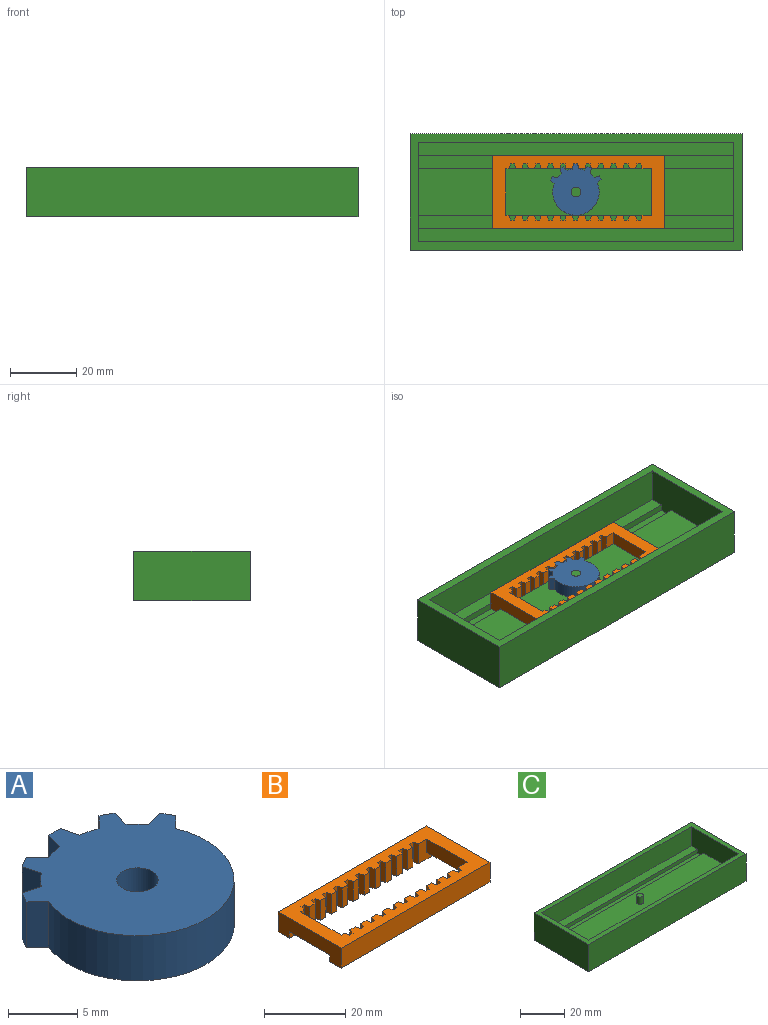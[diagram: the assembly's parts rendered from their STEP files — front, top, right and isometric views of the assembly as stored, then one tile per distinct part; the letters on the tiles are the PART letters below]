
ASSEMBLY  parts=3 mates=4
PART A: 23 faces, bbox 15.3x15.5x4 mm
  f0: plane 15.5x15.29mm, normal (0,0,1), area 158.9mm2, adj f1,f2,f3,f4,f5,f6,f7,f8
  f1: cylinder r=7mm len=14mm, axis (0,0,-1), area 109.3mm2, adj f0,f2,f20,f21
  f2: plane 4x1.14mm, normal (0.7,-0.72,0), area 6.4mm2, adj f0,f1,f3,f21
  f3: cylinder r=8.5mm len=4mm, axis (0,0,-1), area 4.8mm2, adj f0,f2,f4,f21
  f4: plane 4x1.54mm, normal (-0.27,0.96,0), area 6.4mm2, adj f0,f3,f5,f21
  f5: cylinder r=7mm len=4mm, axis (0,0,-1), area 6.6mm2, adj f0,f4,f6,f21
  f6: plane 4x1.54mm, normal (0.96,-0.27,0), area 6.4mm2, adj f0,f5,f7,f21
  f7: cylinder r=8.5mm len=4mm, axis (0,0,-1), area 4.8mm2, adj f0,f6,f8,f21
  f8: plane 4x1.14mm, normal (-0.72,0.7,0), area 6.4mm2, adj f0,f7,f9,f21
  f9: cylinder r=7mm len=4mm, axis (0,0,-1), area 6.6mm2, adj f0,f8,f10,f21
  f10: plane 4x1.55mm, normal (0.97,0.25,0), area 6.4mm2, adj f0,f9,f11,f21
  f11: cylinder r=8.5mm len=4mm, axis (0,0,-1), area 4.8mm2, adj f0,f10,f12,f21
  f12: plane 4x1.55mm, normal (-0.97,0.25,0), area 6.4mm2, adj f0,f11,f13,f21
  f13: cylinder r=7mm len=4mm, axis (0,0,-1), area 6.6mm2, adj f0,f12,f14,f21
  f14: plane 4x1.14mm, normal (0.72,0.7,0), area 6.4mm2, adj f0,f13,f15,f21
  f15: cylinder r=8.5mm len=4mm, axis (0,0,-1), area 4.8mm2, adj f0,f14,f16,f21
  f16: plane 4x1.54mm, normal (-0.96,-0.27,0), area 6.4mm2, adj f0,f15,f17,f21
  f17: cylinder r=7mm len=4mm, axis (0,0,-1), area 6.6mm2, adj f0,f16,f18,f21
  f18: plane 4x1.54mm, normal (0.27,0.96,0), area 6.4mm2, adj f0,f17,f19,f21
  f19: cylinder r=8.5mm len=4mm, axis (0,0,-1), area 4.8mm2, adj f0,f18,f20,f21
  f20: plane 4x1.14mm, normal (-0.7,-0.72,0), area 6.4mm2, adj f0,f1,f19,f21
  f21: plane 15.5x15.29mm, normal (0,0,-1), area 158.9mm2, adj f1,f2,f3,f4,f5,f6,f7,f8
  f22: cylinder r=1.5mm len=4mm, axis (0,0,-1), area 37.7mm2, adj f0,f21
PART B: 101 faces, bbox 52x22x6 mm
  f0: plane 6.92x6mm, normal (0,1,0), area 25.5mm2, adj f3,f41,f83,f87,f89,f94
  f1: cylinder r=8.5mm len=6mm, axis (0,0,1), area 7.3mm2, adj f2,f3,f41,f89
  f2: plane 6x1.48mm, normal (0.97,0.25,0), area 9.2mm2, adj f1,f4,f41,f89
  f3: plane 6x1.48mm, normal (-0.97,0.25,0), area 9.2mm2, adj f0,f1,f41,f89
  f4: plane 6x1.84mm, normal (0,1,0), area 11mm2, adj f2,f7,f41,f89
  f5: cylinder r=8.5mm len=6mm, axis (0,0,1), area 7.3mm2, adj f6,f7,f41,f89
  f6: plane 6x1.48mm, normal (0.97,0.25,0), area 9.2mm2, adj f5,f40,f41,f89
  f7: plane 6x1.48mm, normal (-0.97,0.25,0), area 9.2mm2, adj f4,f5,f41,f89
  f8: plane 6x1.84mm, normal (0,1,0), area 11mm2, adj f11,f14,f41,f89
  f9: cylinder r=8.5mm len=6mm, axis (0,0,1), area 7.3mm2, adj f10,f11,f41,f89
  f10: plane 6x1.48mm, normal (0.97,0.25,0), area 9.2mm2, adj f9,f41,f89,f91
  f11: plane 6x1.48mm, normal (-0.97,0.25,0), area 9.2mm2, adj f8,f9,f41,f89
  f12: plane 6x1.84mm, normal (0,1,0), area 11mm2, adj f15,f18,f41,f89
  f13: cylinder r=8.5mm len=6mm, axis (0,0,1), area 7.3mm2, adj f14,f15,f41,f89
  f14: plane 6x1.48mm, normal (0.97,0.25,0), area 9.2mm2, adj f8,f13,f41,f89
  f15: plane 6x1.48mm, normal (-0.97,0.25,0), area 9.2mm2, adj f12,f13,f41,f89
  f16: plane 6x1.84mm, normal (0,1,0), area 11mm2, adj f19,f22,f41,f89
  f17: cylinder r=8.5mm len=6mm, axis (0,0,1), area 7.3mm2, adj f18,f19,f41,f89
  f18: plane 6x1.48mm, normal (0.97,0.25,0), area 9.2mm2, adj f12,f17,f41,f89
  f19: plane 6x1.48mm, normal (-0.97,0.25,0), area 9.2mm2, adj f16,f17,f41,f89
  f20: plane 6x1.84mm, normal (0,1,0), area 11mm2, adj f23,f26,f41,f89
  f21: cylinder r=8.5mm len=6mm, axis (0,0,1), area 7.3mm2, adj f22,f23,f41,f89
  f22: plane 6x1.48mm, normal (0.97,0.25,0), area 9.2mm2, adj f16,f21,f41,f89
  f23: plane 6x1.48mm, normal (-0.97,0.25,0), area 9.2mm2, adj f20,f21,f41,f89
  f24: plane 6x1.84mm, normal (0,1,0), area 11mm2, adj f27,f30,f41,f89
  f25: cylinder r=8.5mm len=6mm, axis (0,0,1), area 7.3mm2, adj f26,f27,f41,f89
  f26: plane 6x1.48mm, normal (0.97,0.25,0), area 9.2mm2, adj f20,f25,f41,f89
  f27: plane 6x1.48mm, normal (-0.97,0.25,0), area 9.2mm2, adj f24,f25,f41,f89
  f28: plane 6x1.84mm, normal (0,1,0), area 11mm2, adj f31,f34,f41,f89
  f29: cylinder r=8.5mm len=6mm, axis (0,0,1), area 7.3mm2, adj f30,f31,f41,f89
  f30: plane 6x1.48mm, normal (0.97,0.25,0), area 9.2mm2, adj f24,f29,f41,f89
  f31: plane 6x1.48mm, normal (-0.97,0.25,0), area 9.2mm2, adj f28,f29,f41,f89
  f32: plane 6x1.84mm, normal (0,1,0), area 11mm2, adj f35,f38,f41,f89
  f33: cylinder r=8.5mm len=6mm, axis (0,0,1), area 7.3mm2, adj f34,f35,f41,f89
  f34: plane 6x1.48mm, normal (0.97,0.25,0), area 9.2mm2, adj f28,f33,f41,f89
  f35: plane 6x1.48mm, normal (-0.97,0.25,0), area 9.2mm2, adj f32,f33,f41,f89
  f36: plane 6x1.84mm, normal (0,1,0), area 11mm2, adj f39,f41,f89,f100
  f37: cylinder r=8.5mm len=6mm, axis (0,0,1), area 7.3mm2, adj f38,f39,f41,f89
  f38: plane 6x1.48mm, normal (0.97,0.25,0), area 9.2mm2, adj f32,f37,f41,f89
  f39: plane 6x1.48mm, normal (-0.97,0.25,0), area 9.2mm2, adj f36,f37,f41,f89
  f40: plane 6x1.84mm, normal (0,1,0), area 11mm2, adj f6,f41,f89,f99
  f41: plane 52x22mm, normal (0,0,1), area 476mm2, adj f0,f1,f2,f3,f4,f5,f6,f7
  f42: plane 6.92x6mm, normal (0,-1,0), area 25.5mm2, adj f41,f45,f83,f84,f87,f94
  f43: cylinder r=8.5mm len=6mm, axis (0,0,1), area 7.3mm2, adj f41,f44,f45,f84
  f44: plane 6x1.48mm, normal (0.97,-0.25,0), area 9.2mm2, adj f41,f43,f46,f84
  f45: plane 6x1.48mm, normal (-0.97,-0.25,0), area 9.2mm2, adj f41,f42,f43,f84
  f46: plane 6x1.84mm, normal (0,-1,0), area 11mm2, adj f41,f44,f49,f84
  f47: cylinder r=8.5mm len=6mm, axis (0,0,1), area 7.3mm2, adj f41,f48,f49,f84
  f48: plane 6x1.48mm, normal (0.97,-0.25,0), area 9.2mm2, adj f41,f47,f82,f84
  f49: plane 6x1.48mm, normal (-0.97,-0.25,0), area 9.2mm2, adj f41,f46,f47,f84
  f50: plane 6x1.84mm, normal (0,-1,0), area 11mm2, adj f41,f53,f56,f84
  f51: cylinder r=8.5mm len=6mm, axis (0,0,1), area 7.3mm2, adj f41,f52,f53,f84
  f52: plane 6x1.48mm, normal (0.97,-0.25,0), area 9.2mm2, adj f41,f51,f84,f90
  f53: plane 6x1.48mm, normal (-0.97,-0.25,0), area 9.2mm2, adj f41,f50,f51,f84
  f54: plane 6x1.84mm, normal (0,-1,0), area 11mm2, adj f41,f57,f60,f84
  f55: cylinder r=8.5mm len=6mm, axis (0,0,1), area 7.3mm2, adj f41,f56,f57,f84
  f56: plane 6x1.48mm, normal (0.97,-0.25,0), area 9.2mm2, adj f41,f50,f55,f84
  f57: plane 6x1.48mm, normal (-0.97,-0.25,0), area 9.2mm2, adj f41,f54,f55,f84
  f58: plane 6x1.84mm, normal (0,-1,0), area 11mm2, adj f41,f61,f64,f84
  f59: cylinder r=8.5mm len=6mm, axis (0,0,1), area 7.3mm2, adj f41,f60,f61,f84
  f60: plane 6x1.48mm, normal (0.97,-0.25,0), area 9.2mm2, adj f41,f54,f59,f84
  f61: plane 6x1.48mm, normal (-0.97,-0.25,0), area 9.2mm2, adj f41,f58,f59,f84
  f62: plane 6x1.84mm, normal (0,-1,0), area 11mm2, adj f41,f65,f68,f84
  f63: cylinder r=8.5mm len=6mm, axis (0,0,1), area 7.3mm2, adj f41,f64,f65,f84
  f64: plane 6x1.48mm, normal (0.97,-0.25,0), area 9.2mm2, adj f41,f58,f63,f84
  f65: plane 6x1.48mm, normal (-0.97,-0.25,0), area 9.2mm2, adj f41,f62,f63,f84
  f66: plane 6x1.84mm, normal (0,-1,0), area 11mm2, adj f41,f69,f72,f84
  f67: cylinder r=8.5mm len=6mm, axis (0,0,1), area 7.3mm2, adj f41,f68,f69,f84
  f68: plane 6x1.48mm, normal (0.97,-0.25,0), area 9.2mm2, adj f41,f62,f67,f84
  f69: plane 6x1.48mm, normal (-0.97,-0.25,0), area 9.2mm2, adj f41,f66,f67,f84
  f70: plane 6x1.84mm, normal (0,-1,0), area 11mm2, adj f41,f73,f76,f84
  f71: cylinder r=8.5mm len=6mm, axis (0,0,1), area 7.3mm2, adj f41,f72,f73,f84
  f72: plane 6x1.48mm, normal (0.97,-0.25,0), area 9.2mm2, adj f41,f66,f71,f84
  f73: plane 6x1.48mm, normal (-0.97,-0.25,0), area 9.2mm2, adj f41,f70,f71,f84
  f74: plane 6x1.84mm, normal (0,-1,0), area 11mm2, adj f41,f77,f80,f84
  f75: cylinder r=8.5mm len=6mm, axis (0,0,1), area 7.3mm2, adj f41,f76,f77,f84
  f76: plane 6x1.48mm, normal (0.97,-0.25,0), area 9.2mm2, adj f41,f70,f75,f84
  f77: plane 6x1.48mm, normal (-0.97,-0.25,0), area 9.2mm2, adj f41,f74,f75,f84
  f78: plane 6x1.84mm, normal (0,-1,0), area 11mm2, adj f41,f81,f84,f96
  f79: cylinder r=8.5mm len=6mm, axis (0,0,1), area 7.3mm2, adj f41,f80,f81,f84
  f80: plane 6x1.48mm, normal (0.97,-0.25,0), area 9.2mm2, adj f41,f74,f79,f84
  f81: plane 6x1.48mm, normal (-0.97,-0.25,0), area 9.2mm2, adj f41,f78,f79,f84
  f82: plane 6x1.84mm, normal (0,-1,0), area 11mm2, adj f41,f48,f84,f97
  f83: plane 14x4mm, normal (0,0,-1), area 56mm2, adj f0,f42,f87,f94
  f84: plane 52x4mm, normal (0,0,-1), area 182mm2, adj f42,f43,f44,f45,f46,f47,f48,f49
  f85: plane 22x6mm, normal (-1,0,0), area 104mm2, adj f41,f84,f86,f88,f89,f90,f91,f92
  f86: plane 52x6mm, normal (0,-1,0), area 312mm2, adj f41,f85,f87,f89
  f87: plane 22x6mm, normal (1,0,0), area 104mm2, adj f0,f41,f42,f83,f84,f86,f88,f89
  f88: plane 52x6mm, normal (0,1,0), area 312mm2, adj f41,f84,f85,f87
  f89: plane 52x4mm, normal (0,0,-1), area 182mm2, adj f0,f1,f2,f3,f4,f5,f6,f7
  f90: plane 6x5.12mm, normal (0,-1,0), area 14.7mm2, adj f41,f52,f84,f85,f92,f93
  f91: plane 6x5.12mm, normal (0,1,0), area 14.7mm2, adj f10,f41,f85,f89,f92,f93
  f92: plane 14x4mm, normal (0,0,-1), area 56mm2, adj f85,f90,f91,f93
  f93: plane 14x4mm, normal (1,0,0), area 56mm2, adj f41,f90,f91,f92
  f94: plane 14x4mm, normal (-1,0,0), area 56mm2, adj f0,f41,f42,f83
  f95: cylinder r=8.5mm len=6mm, axis (0,0,1), area 7.3mm2, adj f41,f84,f96,f97
  f96: plane 6x1.48mm, normal (0.97,-0.25,0), area 9.2mm2, adj f41,f78,f84,f95
  f97: plane 6x1.48mm, normal (-0.97,-0.25,0), area 9.2mm2, adj f41,f82,f84,f95
  f98: cylinder r=8.5mm len=6mm, axis (0,0,1), area 7.3mm2, adj f41,f89,f99,f100
  f99: plane 6x1.48mm, normal (-0.97,0.25,0), area 9.2mm2, adj f40,f41,f89,f98
  f100: plane 6x1.48mm, normal (0.97,0.25,0), area 9.2mm2, adj f36,f41,f89,f98
PART C: 21 faces, bbox 100x35x15 mm
  f0: plane 95x4mm, normal (0,0,1), area 380mm2, adj f1,f10,f12,f16
  f1: plane 30x12.5mm, normal (1,0,0), area 331mm2, adj f0,f2,f3,f9,f11,f12,f13,f14
  f2: plane 95x4mm, normal (0,0,1), area 380mm2, adj f1,f10,f14,f17
  f3: plane 100x35mm, normal (0,0,1), area 650mm2, adj f1,f4,f5,f6,f7,f9,f10,f11
  f4: plane 35x15mm, normal (-1,0,0), area 525mm2, adj f3,f5,f7,f8
  f5: plane 100x15mm, normal (0,-1,0), area 1500mm2, adj f3,f4,f6,f8
  f6: plane 35x15mm, normal (1,0,0), area 525mm2, adj f3,f5,f7,f8
  f7: plane 100x15mm, normal (0,1,0), area 1500mm2, adj f3,f4,f6,f8
  f8: plane 100x35mm, normal (0,0,-1), area 3500mm2, adj f4,f5,f6,f7
  f9: plane 95x10.5mm, normal (0,1,0), area 997.5mm2, adj f1,f3,f10,f15
  f10: plane 30x12.5mm, normal (-1,0,0), area 331mm2, adj f0,f2,f3,f9,f11,f12,f13,f14
  f11: plane 95x10.5mm, normal (0,-1,0), area 997.5mm2, adj f1,f3,f10,f13
  f12: plane 95x2mm, normal (0,-1,0), area 190mm2, adj f0,f1,f10,f13
  f13: plane 95x4mm, normal (0,0,1), area 380mm2, adj f1,f10,f11,f12
  f14: plane 95x2mm, normal (0,1,0), area 190mm2, adj f1,f2,f10,f15
  f15: plane 95x4mm, normal (0,0,1), area 380mm2, adj f1,f9,f10,f14
  f16: plane 95x2mm, normal (0,1,0), area 190mm2, adj f0,f1,f10,f18
  f17: plane 95x2mm, normal (0,-1,0), area 190mm2, adj f1,f2,f10,f18
  f18: plane 95x14mm, normal (0,0,1), area 1322.9mm2, adj f1,f10,f16,f17,f20
  f19: plane 3x3mm, normal (0,0,1), area 7.1mm2, adj f20
  f20: cylinder r=1.5mm len=4mm, axis (0,0,-1), area 37.7mm2, adj f18,f19
PLACE A rot(axis=(0,0,1),1deg) t=(-28.59,-18.82,20.5)mm
PLACE B t=(-17.6,-17.98,20.5)mm
PLACE C t=(-28.89,-17.98,20.5)mm fixed
MATE planar B.f88 <-> C.f12  axis (0,1,0) through (21.9,10.52,26)mm
MATE planar C.f20 <-> A.f0  axis (0,0,1) through (21.11,-0.48,29)mm
MATE planar C.f0 <-> B.f84  axis (0,0,1) through (21.11,8.52,23)mm
MATE cylindrical C.f20 <-> A.f1  axis (0,0,-1) through (21.11,-0.48,27)mm
